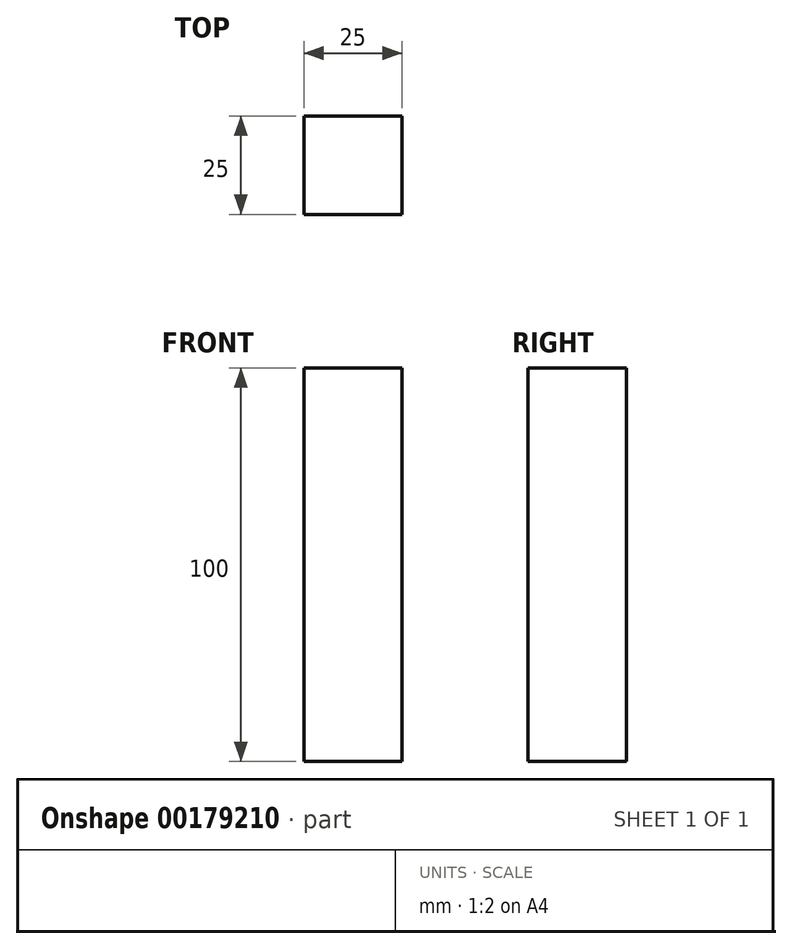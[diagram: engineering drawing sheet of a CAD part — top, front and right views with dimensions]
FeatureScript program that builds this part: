
annotation { "Feature Type Name" : "Feature", "Feature Type Description" : "" }
export const myFeature = defineFeature(function(context is Context, id is Id, definition is map)
    precondition{}
    {
        {
            var Q0;
            Q0=qCreatedBy(makeId("Top.planeOp"),FACE);
            var sketch = newSketch(context, id + "F0", { "sketchPlane" : qUnion([Q0])});
            skLineSegment(sketch, "E0.bottom", {"start": v(-7.42, -1.62) * mm, "end": v(17.58, -1.62) * mm});
            skLineSegment(sketch, "E0.top", {"start": v(-7.42, -26.62) * mm, "end": v(17.58, -26.62) * mm});
            skLineSegment(sketch, "E0.left", {"start": v(-7.42, -1.62) * mm, "end": v(-7.42, -26.62) * mm});
            skLineSegment(sketch, "E0.right", {"start": v(17.58, -1.62) * mm, "end": v(17.58, -26.62) * mm});
            skSolve(sketch);
        }
        {
            var Q0;
            Q0=makeQuery(id+"F0.imprint","IMPRINT",FACE,{"disambiguationData":[TD([[makeQuery(id+"F0.imprint","IMPRINT",EDGE,{"derivedFrom":sQuery(id+"F0.wireOp",EDGE,"E0.bottom")}),-1.0]])]});
            extrude(context, id + "F1", {"entities" : qUnion([Q0]), "depth" : 100 * mm});
        }
    });
